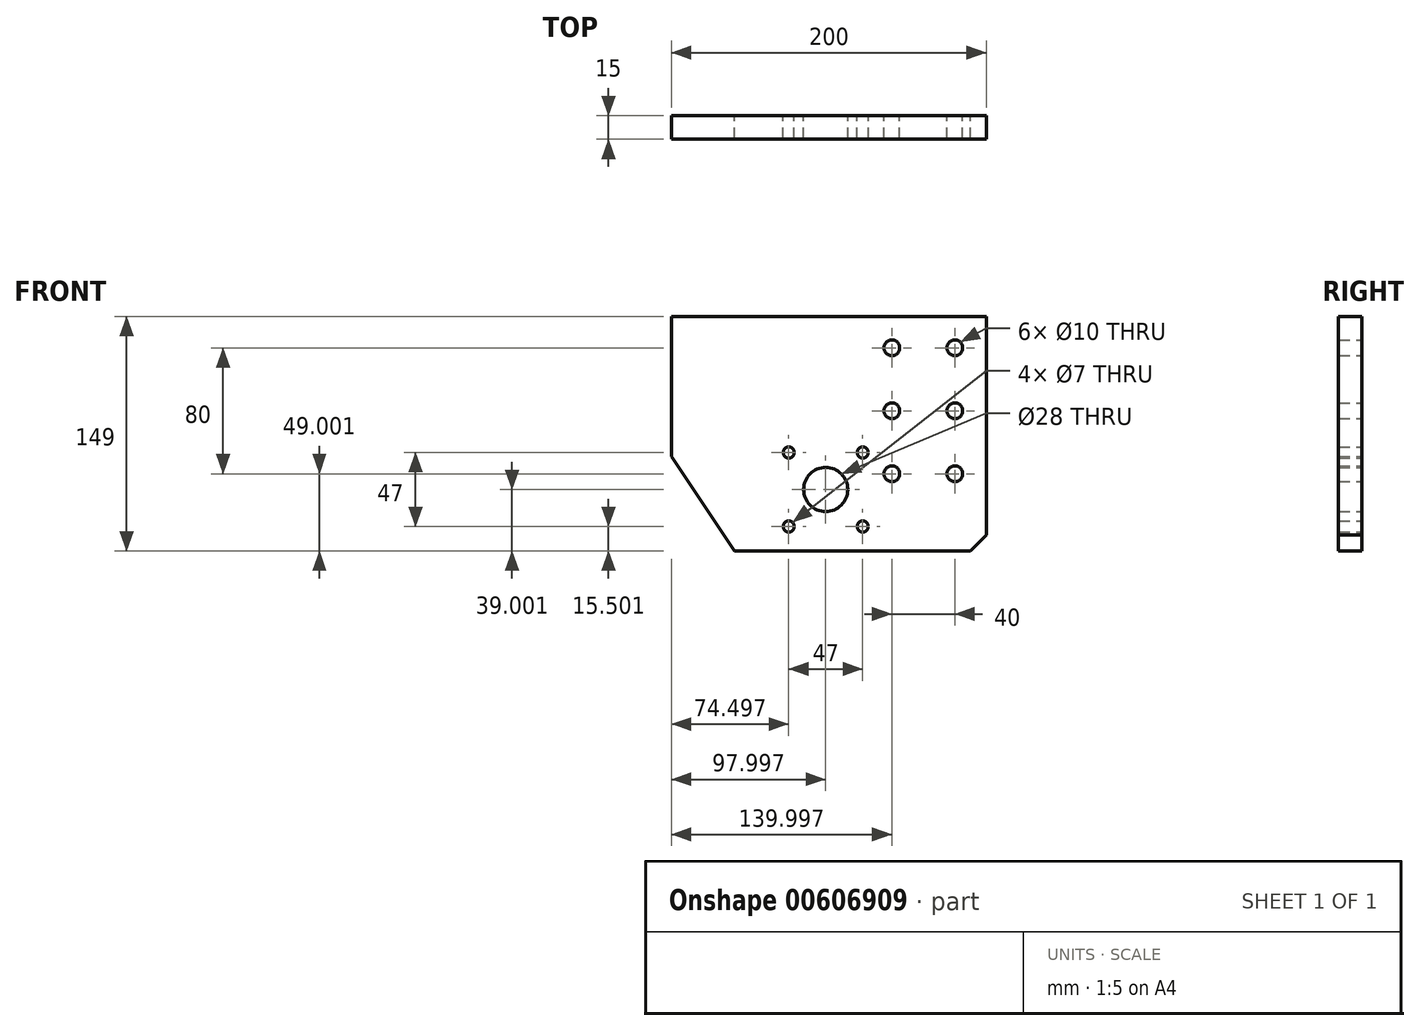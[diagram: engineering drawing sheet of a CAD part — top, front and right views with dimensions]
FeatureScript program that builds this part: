
annotation { "Feature Type Name" : "Feature", "Feature Type Description" : "" }
export const myFeature = defineFeature(function(context is Context, id is Id, definition is map)
    precondition{}
    {
        {
            var Q0;
            Q0=qCreatedBy(makeId("Front.planeOp"),FACE);
            var sketch = newSketch(context, id + "F0", { "sketchPlane" : qUnion([Q0]) });
            skLineSegment(sketch, "E0.0", {"start": v(77.65, -54.53) * mm, "end": v(77.65, 84.47) * mm});
            skLineSegment(sketch, "E1.0", {"start": v(77.65, -54.53) * mm, "end": v(67.65, -64.53) * mm});
            skLineSegment(sketch, "E2.0", {"start": v(-82.35, -64.53) * mm, "end": v(67.65, -64.53) * mm});
            skLineSegment(sketch, "E3.0", {"start": v(-82.35, -64.53) * mm, "end": v(-122.35, -4.53) * mm});
            skLineSegment(sketch, "E4.0", {"start": v(-122.35, -4.53) * mm, "end": v(-122.35, 84.47) * mm});
            skLineSegment(sketch, "E5.0", {"start": v(-122.35, 84.47) * mm, "end": v(77.65, 84.47) * mm});
            skCircle(sketch, "E6.0", {"center": v(-0.85, -49.03) * mm, "radius": 3.5 * mm});
            skCircle(sketch, "E7.0", {"center": v(-47.85, -49.03) * mm, "radius": 3.5 * mm});
            skCircle(sketch, "E8.0", {"center": v(-47.85, -2.03) * mm, "radius": 3.5 * mm});
            skCircle(sketch, "E9.0", {"center": v(57.65, 64.47) * mm, "radius": 5 * mm});
            skCircle(sketch, "E10.0", {"center": v(57.65, 24.47) * mm, "radius": 5 * mm});
            skCircle(sketch, "E11.0", {"center": v(57.65, -15.53) * mm, "radius": 5 * mm});
            skCircle(sketch, "E12.0", {"center": v(17.65, -15.53) * mm, "radius": 5 * mm});
            skCircle(sketch, "E13.0", {"center": v(-0.85, -2.03) * mm, "radius": 3.5 * mm});
            skCircle(sketch, "E14.0", {"center": v(17.65, 24.47) * mm, "radius": 5 * mm});
            skCircle(sketch, "E15.0", {"center": v(17.65, 64.47) * mm, "radius": 5 * mm});
            skPoint(sketch, "E16", {"position": v(-24.35, -25.53) * mm});
            skCircle(sketch, "E17", {"center": v(-24.35, -25.53) * mm, "radius": 14 * mm});
            skSolve(sketch);
        }
        {
            var Q0;
            Q0=makeQuery(id+"F0.imprint","IMPRINT",FACE,{"disambiguationData":[TD([[makeQuery(id+"F0.imprint","IMPRINT",EDGE,{"derivedFrom":sQuery(id+"F0.wireOp",EDGE,"E0.0")}),1.0]])]});
            extrude(context, id + "F1", {"entities" : qUnion([Q0]), "depth" : 15 * mm, "offsetDistance" : 25 * mm});
        }
    });
